# Revit family: Reece_Shower_Milli_Inox_Freestanding Twin Shower_Microphone Head with
name_source: partatom
category: Plumbing Fixtures
revit_build: Autodesk Revit 2018 (Build: 20190510_1515(x64)
units: mm (PartAtom-declared; Revit-internal decimal feet)

## family parameters
Cut with Voids When Loaded = No
Host = Face
Part Type = Normal
Room Calculation Point = Yes
Round Connector Dimension = Use Diameter
Shared = Yes

## types (1)
- Brushed Stainless Steel
    CWFU = 0
    Default Elevation = 1000 mm  [stored 3.28084 ft]
    Description = Milli Inox Freestanding Twin Shower Stainless Steel (3 Star)
    Disclaimer = THIS FILE IS THE PROPERTY OF THE REECE GROUP. IT MAY NOT BE REPRODUCED, REVERSE-ENGINEERED OR MODIFIED. ANY REPUBLICATION, TRANSMISSION OR DISTRIBUTION FOR THE PURPOSE OF COMMERCIALLY EXPLOITING THE FILES IS PROHIBITED.
    HWFU = 0
    Keynote = Product #2252113, Reece_Shower_Milli_Inox_Freestanding Twin Shower_Microphone Head with - Brushed Stainless Steel
    Manufacturer = Milli
    Model = Inox
    Reece_Detail_Additional = Microphone Head with Handshower
    Reece_Detail_Disclaimer = THIS FILE IS THE PROPERTY OF THE REECE GROUP. IT MAY NOT BE REPRODUCED, REVERSE-ENGINEERED OR MODIFIED. ANY REPUBLICATION, TRANSMISSION OR DISTRIBUTION FOR THE PURPOSE OF COMMERCIALLY EXPLOITING THE FILES IS PROHIBITED.
    Reece_Detail_Installation = Freestanding Twin Shower
    Reece_Material-Main = Reece_Brass_Brushed Stainless Steel
    Reece_Overall_Height = 2072 mm  [stored 6.7979 ft]
    Reece_Product_Brand = Milli
    Reece_Product_Description = Milli Inox Freestanding Twin Shower Stainless Steel (3 Star)
    Reece_Product_Mount = Floor Mounted
    Reece_Product_Number = 2252113
    Reece_Product_Sub Brand = Inox
    Reece_Product_Type = Shower
    Reece_Product_Web Page = https://www.reece.com.au
    Reece_Shower_Inlet = 13 mm  [stored 0.0426509 ft]
    Reece_Shower_Reach = 457 mm  [stored 1.49934 ft]
    Type Comments = Shower
    URL = https://www.reece.com.au
    WFU = 0

note: [stored X ft] marks values corroborated as IEEE doubles in the binary element streams (Revit-internal decimal feet)

## geometry (parser evidence)
native form markers: Sweep x5
no freeform markers — native parametric forms only
